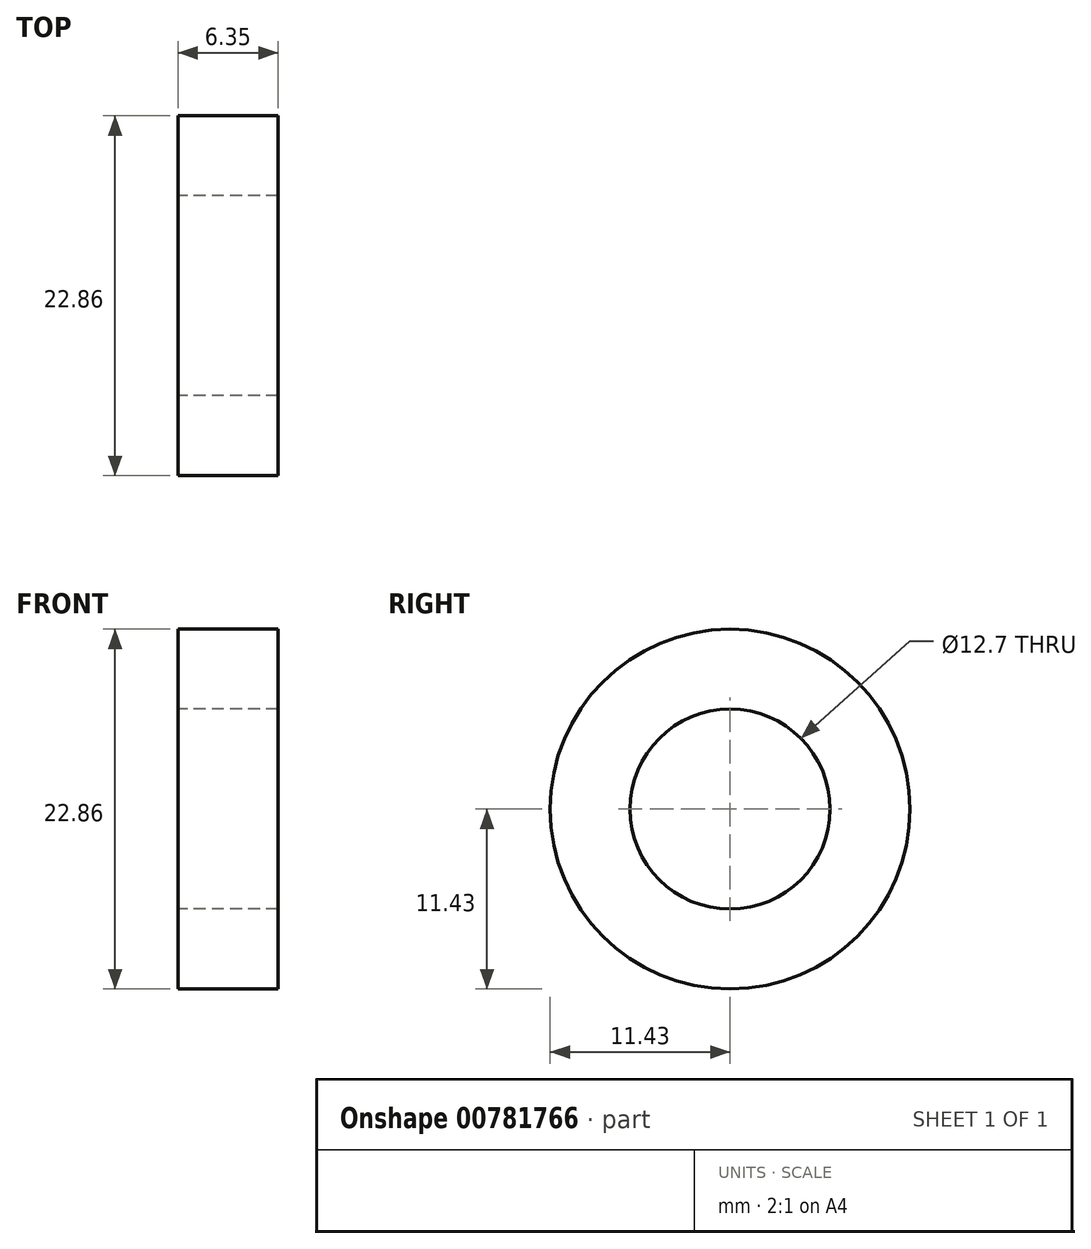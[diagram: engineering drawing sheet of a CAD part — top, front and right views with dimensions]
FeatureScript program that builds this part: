
annotation { "Feature Type Name" : "Feature", "Feature Type Description" : "" }
export const myFeature = defineFeature(function(context is Context, id is Id, definition is map)
    precondition{}
    {
        {
            var Q0;
            Q0=qCreatedBy(makeId("Top.planeOp"),FACE);
            var sketch = newSketch(context, id + "F0", { "sketchPlane" : qUnion([Q0])});
            skLineSegment(sketch, "E0.bottom", {"start": v(31.75, -31.75) * mm, "end": v(-31.75, -31.75) * mm});
            skLineSegment(sketch, "E0.top", {"start": v(31.75, 31.75) * mm, "end": v(-31.75, 31.75) * mm});
            skLineSegment(sketch, "E0.left", {"start": v(31.75, -31.75) * mm, "end": v(31.75, 31.75) * mm});
            skLineSegment(sketch, "E0.right", {"start": v(-31.75, -31.75) * mm, "end": v(-31.75, 31.75) * mm});
            skPoint(sketch, "E0.middle", {"position": v(0, 0) * mm});
            skLineSegment(sketch, "E1.bottom", {"start": v(25.4, -25.4) * mm, "end": v(-25.4, -25.4) * mm});
            skLineSegment(sketch, "E1.top", {"start": v(25.4, 25.4) * mm, "end": v(-25.4, 25.4) * mm});
            skLineSegment(sketch, "E1.left", {"start": v(25.4, -25.4) * mm, "end": v(25.4, 25.4) * mm});
            skLineSegment(sketch, "E1.right", {"start": v(-25.4, -25.4) * mm, "end": v(-25.4, 25.4) * mm});
            skSolve(sketch);
        }
        {
            var Q0;
            Q0=makeQuery(id+"F0.imprint","IMPRINT",FACE,{"disambiguationData":[TD([[makeQuery(id+"F0.imprint","IMPRINT",EDGE,{"derivedFrom":sQuery(id+"F0.wireOp",EDGE,"E0.bottom")}),-1.0]])]});
            extrude(context, id + "F1", {"entities" : qUnion([Q0]), "endBound" : BoundingType.SYMMETRIC, "depth" : 330.2 * mm, "offsetDistance" : 25.4 * mm});
        }
        {
            var Q0;
            Q0=makeQuery(id+"F1.opExtrude","SWEPT_FACE",FACE,{"disambiguationData":[OSD([sQuery(id+"F0.wireOp",EDGE,"E0.right")])]});
            var sketch = newSketch(context, id + "F2", { "sketchPlane" : qUnion([Q0])});
            skSolve(sketch);
        }
        {
            var Q0;
            Q0=makeQuery(id+"F1.opExtrude","SWEPT_FACE",FACE,{"disambiguationData":[OSD([sQuery(id+"F0.wireOp",EDGE,"E0.left")])]});
            var sketch = newSketch(context, id + "F3", { "sketchPlane" : qUnion([Q0])});
            skLineSegment(sketch, "E2.0", {"start": v(-31.75, 165.1) * mm, "end": v(31.75, 165.1) * mm, "construction": true});
            skLineSegment(sketch, "E2.1", {"start": v(-31.75, 165.1) * mm, "end": v(-31.75, -165.1) * mm, "construction": true});
            skLineSegment(sketch, "E2.2", {"start": v(31.75, 165.1) * mm, "end": v(31.75, -165.1) * mm, "construction": true});
            skLineSegment(sketch, "E2.3", {"start": v(-31.75, -165.1) * mm, "end": v(31.75, -165.1) * mm, "construction": true});
            skCircle(sketch, "E3", {"center": v(0, 146.05) * mm, "radius": 6.35 * mm});
            skArc(sketch, "E4", {"start": v(17.84, 137.73) * mm, "mid": v(19.5, 143.31) * mm, "end": v(19.44, 149.13) * mm});
            skArc(sketch, "E5", {"start": v(10.93, 140.95) * mm, "mid": v(11.95, 144.37) * mm, "end": v(11.92, 147.94) * mm});
            skLineSegment(sketch, "E6", {"start": v(0, 146.05) * mm, "end": v(19.44, 149.13) * mm, "construction": true});
            skLineSegment(sketch, "E7", {"start": v(0, 146.05) * mm, "end": v(9.54, 128.83) * mm, "construction": true});
            skLineSegment(sketch, "E8", {"start": v(0, 146.05) * mm, "end": v(24.19, 134.77) * mm, "construction": true});
            skCircle(sketch, "E9", {"center": v(0, 146.05) * mm, "radius": 15.88 * mm, "construction": true});
            skArc(sketch, "E10", {"start": v(11.92, 147.94) * mm, "mid": v(15.08, 152.3) * mm, "end": v(19.44, 149.13) * mm});
            skArc(sketch, "E11.MirrorCS", {"start": v(6.21, 135.7) * mm, "mid": v(4.91, 130.48) * mm, "end": v(10.14, 129.18) * mm});
            skArc(sketch, "E12.MirrorCS", {"start": v(10.93, 140.95) * mm, "mid": v(8.97, 137.98) * mm, "end": v(6.21, 135.7) * mm});
            skArc(sketch, "E13.MirrorCS", {"start": v(17.84, 137.73) * mm, "mid": v(14.63, 132.88) * mm, "end": v(10.14, 129.18) * mm});
            skLineSegment(sketch, "E14", {"start": v(0, 146.05) * mm, "end": v(-19.11, 146.05) * mm, "construction": true});
            skLineSegment(sketch, "E15", {"start": v(0, 146.05) * mm, "end": v(0, 119.4) * mm, "construction": true});
            skArc(sketch, "E16.MirrorCS", {"start": v(-6.21, 135.7) * mm, "mid": v(-4.91, 130.48) * mm, "end": v(-10.14, 129.18) * mm});
            skArc(sketch, "E17.MirrorCS", {"start": v(-17.84, 137.73) * mm, "mid": v(-14.63, 132.88) * mm, "end": v(-10.14, 129.18) * mm});
            skArc(sketch, "E18.MirrorCS", {"start": v(-17.84, 137.73) * mm, "mid": v(-19.5, 143.31) * mm, "end": v(-19.44, 149.13) * mm});
            skArc(sketch, "E19.MirrorCS", {"start": v(-11.92, 147.94) * mm, "mid": v(-15.08, 152.3) * mm, "end": v(-19.44, 149.13) * mm});
            skArc(sketch, "E20.MirrorCS", {"start": v(-10.93, 140.95) * mm, "mid": v(-11.95, 144.37) * mm, "end": v(-11.92, 147.94) * mm});
            skArc(sketch, "E21.MirrorCS", {"start": v(-10.93, 140.95) * mm, "mid": v(-8.97, 137.98) * mm, "end": v(-6.21, 135.7) * mm});
            skSolve(sketch);
        }
        {
            var Q0;
            Q0=makeQuery(id+"F3.imprint","IMPRINT",FACE,{"disambiguationData":[TD([[makeQuery(id+"F3.imprint","IMPRINT",EDGE,{"derivedFrom":sQuery(id+"F3.wireOp",EDGE,"E3")}),1.0]])]});
            var Q1;
            Q1=makeQuery(id+"F3.imprint","IMPRINT",FACE,{"disambiguationData":[TD([[makeQuery(id+"F3.imprint","IMPRINT",EDGE,{"derivedFrom":sQuery(id+"F3.wireOp",EDGE,"E4")}),1.0]])]});
            var Q2;
            Q2=makeQuery(id+"F3.imprint","IMPRINT",FACE,{"disambiguationData":[TD([[makeQuery(id+"F3.imprint","IMPRINT",EDGE,{"derivedFrom":sQuery(id+"F3.wireOp",EDGE,"E16.MirrorCS")}),-1.0]])]});
            extrude(context, id + "F4", {"entities" : qUnion([Q0, Q1, Q2]), "operationType" : NewBodyOperationType.REMOVE, "oppositeDirection" : true, "depth" : 25.4 * mm, "offsetDistance" : 25.4 * mm});
        }
        {
            var Q0;
            {var subQ0=sQuery(id+"F0.wireOp",EDGE,"E0.right");Q0=makeQuery(id+"F2.imprint","IMPRINT",FACE,{"disambiguationData":[TD([[makeQuery(id+"F2.imprint","IMPRINT",EDGE,{"derivedFrom":makeQuery(id+"F1.opExtrude","CAP_EDGE",EDGE,{"disambiguationData":[OSD([subQ0])],"isStart":true})}),-1.0]])]});}
            var sketch = newSketch(context, id + "F5", { "sketchPlane" : qUnion([Q0])});
            skCircle(sketch, "E22.0", {"center": v(0, 146.05) * mm, "radius": 6.35 * mm});
            skCircle(sketch, "E23", {"center": v(-7.7, 132.17) * mm, "radius": 1.9 * mm});
            skArc(sketch, "E24", {"start": v(5.1, 127.04) * mm, "mid": v(17.84, 137.73) * mm, "end": v(17.84, 154.37) * mm});
            skCircle(sketch, "E25", {"center": v(0, 146.05) * mm, "radius": 15.88 * mm, "construction": true});
            skLineSegment(sketch, "E26", {"start": v(0, 146.05) * mm, "end": v(5.1, 127.04) * mm, "construction": true});
            skLineSegment(sketch, "E27", {"start": v(0, 146.05) * mm, "end": v(-15.88, 146.05) * mm, "construction": true});
            skLineSegment(sketch, "E28", {"start": v(0, 146.05) * mm, "end": v(17.84, 154.37) * mm, "construction": true});
            skArc(sketch, "E29", {"start": v(3.12, 134.4) * mm, "mid": v(10.93, 140.95) * mm, "end": v(10.93, 151.15) * mm});
            skLineSegment(sketch, "E30", {"start": v(0, 146.05) * mm, "end": v(-7.7, 132.17) * mm});
            skArc(sketch, "E31", {"start": v(3.12, 134.4) * mm, "mid": v(0.43, 129.73) * mm, "end": v(5.1, 127.04) * mm});
            skArc(sketch, "E32", {"start": v(17.84, 154.37) * mm, "mid": v(12.78, 156.21) * mm, "end": v(10.93, 151.15) * mm});
            skCircle(sketch, "E33", {"center": v(-7.7, 132.17) * mm, "radius": 3.18 * mm, "construction": true});
            skLineSegment(sketch, "E34", {"start": v(0, 146.05) * mm, "end": v(-15.58, 149.08) * mm, "construction": true});
            skCircle(sketch, "E35", {"center": v(-15.58, 149.08) * mm, "radius": 3.18 * mm, "construction": true});
            skArc(sketch, "E36.0", {"start": v(-11.92, 147.94) * mm, "mid": v(-15.08, 152.3) * mm, "end": v(-19.44, 149.13) * mm, "construction": true});
            skLineSegment(sketch, "E37", {"start": v(0, 146.05) * mm, "end": v(-15.68, 148.53) * mm, "construction": true});
            skSolve(sketch);
        }
        {
            var Q0;
            Q0=qSketchRegion(id+"F5",true);
            extrude(context, id + "F6", {"entities" : qUnion([Q0]), "operationType" : NewBodyOperationType.REMOVE, "oppositeDirection" : true, "depth" : 25.4 * mm, "offsetDistance" : 25.4 * mm});
        }
        {
            var Q0;
            Q0=makeQuery(id+"F1.opExtrude","SWEPT_FACE",FACE,{"disambiguationData":[OSD([sQuery(id+"F0.wireOp",EDGE,"E0.left")])]});
            var sketch = newSketch(context, id + "F7", { "sketchPlane" : qUnion([Q0])});
            skArc(sketch, "E38", {"start": v(-8.89, 101.6) * mm, "mid": v(10.16, 82.55) * mm, "end": v(-8.89, 63.5) * mm, "construction": true});
            skArc(sketch, "E39.0", {"start": v(-8.89, 95.25) * mm, "mid": v(3.81, 82.55) * mm, "end": v(-8.89, 69.85) * mm});
            skArc(sketch, "E40.0", {"start": v(-8.89, 107.95) * mm, "mid": v(16.5, 82.55) * mm, "end": v(-8.89, 57.15) * mm});
            skArc(sketch, "E41", {"start": v(-8.89, 107.95) * mm, "mid": v(-15.24, 101.6) * mm, "end": v(-8.89, 95.25) * mm});
            skArc(sketch, "E42", {"start": v(-8.89, 57.15) * mm, "mid": v(-15.24, 63.5) * mm, "end": v(-8.89, 69.85) * mm});
            skArc(sketch, "E43", {"start": v(8.9, 6.35) * mm, "mid": v(-10.16, 25.4) * mm, "end": v(8.9, 44.45) * mm, "construction": true});
            skArc(sketch, "E44.0", {"start": v(8.9, 12.7) * mm, "mid": v(-3.8, 25.4) * mm, "end": v(8.9, 38.1) * mm});
            skArc(sketch, "E45.0", {"start": v(8.9, 0) * mm, "mid": v(-16.5, 25.4) * mm, "end": v(8.89, 50.8) * mm});
            skArc(sketch, "E46", {"start": v(8.9, 0) * mm, "mid": v(15.24, 6.35) * mm, "end": v(8.9, 12.7) * mm});
            skArc(sketch, "E47", {"start": v(8.9, 50.8) * mm, "mid": v(15.24, 44.45) * mm, "end": v(8.9, 38.1) * mm});
            skArc(sketch, "E48", {"start": v(-8.89, -12.7) * mm, "mid": v(10.16, -31.75) * mm, "end": v(-8.89, -50.8) * mm, "construction": true});
            skArc(sketch, "E49.0", {"start": v(-8.89, -19.05) * mm, "mid": v(3.81, -31.75) * mm, "end": v(-8.89, -44.45) * mm});
            skArc(sketch, "E50.0", {"start": v(-8.89, -6.35) * mm, "mid": v(16.5, -31.75) * mm, "end": v(-8.89, -57.15) * mm});
            skArc(sketch, "E51", {"start": v(-8.89, -6.35) * mm, "mid": v(-15.24, -12.7) * mm, "end": v(-8.89, -19.05) * mm});
            skArc(sketch, "E52", {"start": v(-8.89, -57.15) * mm, "mid": v(-15.24, -50.8) * mm, "end": v(-8.89, -44.45) * mm});
            skArc(sketch, "E53", {"start": v(8.9, -107.95) * mm, "mid": v(-10.16, -88.9) * mm, "end": v(8.89, -69.85) * mm, "construction": true});
            skArc(sketch, "E54.0", {"start": v(8.9, -101.6) * mm, "mid": v(-3.8, -88.9) * mm, "end": v(8.89, -76.2) * mm});
            skArc(sketch, "E55.0", {"start": v(8.9, -114.3) * mm, "mid": v(-16.5, -88.9) * mm, "end": v(8.89, -63.5) * mm});
            skArc(sketch, "E56", {"start": v(8.9, -114.3) * mm, "mid": v(15.24, -107.95) * mm, "end": v(8.9, -101.6) * mm});
            skArc(sketch, "E57", {"start": v(8.89, -63.5) * mm, "mid": v(15.24, -69.85) * mm, "end": v(8.89, -76.2) * mm});
            skCircle(sketch, "E58", {"center": v(-8.89, 82.55) * mm, "radius": 6.35 * mm});
            skCircle(sketch, "E59", {"center": v(8.9, 25.4) * mm, "radius": 6.35 * mm});
            skCircle(sketch, "E60", {"center": v(8.9, -88.9) * mm, "radius": 6.35 * mm});
            skCircle(sketch, "E61", {"center": v(-8.89, -31.75) * mm, "radius": 6.35 * mm});
            skSolve(sketch);
        }
        {
            var Q0;
            Q0=qSketchRegion(id+"F7",true);
            extrude(context, id + "F8", {"entities" : qUnion([Q0]), "operationType" : NewBodyOperationType.REMOVE, "endBound" : BoundingType.THROUGH_ALL, "oppositeDirection" : true, "depth" : 25.4 * mm, "offsetDistance" : 25.4 * mm});
        }
        {
            var Q0;
            Q0=makeQuery(id+"F1.opExtrude","SWEPT_FACE",FACE,{"disambiguationData":[OSD([sQuery(id+"F0.wireOp",EDGE,"E1.left")])]});
            var sketch = newSketch(context, id + "F9", { "sketchPlane" : qUnion([Q0])});
            skLineSegment(sketch, "E62.bottom", {"start": v(-25.4, 165.1) * mm, "end": v(25.4, 165.1) * mm});
            skLineSegment(sketch, "E62.top", {"start": v(-25.4, -127) * mm, "end": v(25.4, -127) * mm});
            skLineSegment(sketch, "E62.left", {"start": v(-25.4, 165.1) * mm, "end": v(-25.4, -127) * mm});
            skLineSegment(sketch, "E62.right", {"start": v(25.4, 165.1) * mm, "end": v(25.4, -127) * mm});
            skLineSegment(sketch, "E63.bottom", {"start": v(72.9, -188.97) * mm, "end": v(-72.9, -188.97) * mm});
            skLineSegment(sketch, "E63.top", {"start": v(72.9, 188.97) * mm, "end": v(-72.9, 188.97) * mm});
            skLineSegment(sketch, "E63.left", {"start": v(72.9, -188.97) * mm, "end": v(72.9, 188.97) * mm});
            skLineSegment(sketch, "E63.right", {"start": v(-72.9, -188.97) * mm, "end": v(-72.9, 188.97) * mm});
            skPoint(sketch, "E63.middle", {"position": v(0, 0) * mm});
            skSolve(sketch);
        }
        {
            var Q0;
            Q0=qSketchRegion(id+"F9",true);
            extrude(context, id + "F10", {"entities" : qUnion([Q0]), "operationType" : NewBodyOperationType.REMOVE, "endBound" : BoundingType.SYMMETRIC, "oppositeDirection" : true, "depth" : 127 * mm, "offsetDistance" : 25.4 * mm});
        }
        {
            var Q0;
            Q0=makeQuery(id+"F1.opExtrude","SWEPT_FACE",FACE,{"disambiguationData":[OSD([sQuery(id+"F0.wireOp",EDGE,"E1.right")])]});
            var sketch = newSketch(context, id + "F11", { "sketchPlane" : qUnion([Q0])});
            skLineSegment(sketch, "E64.bottom", {"start": v(-48.84, -169.45) * mm, "end": v(48.84, -169.45) * mm});
            skLineSegment(sketch, "E64.top", {"start": v(-48.84, 169.45) * mm, "end": v(48.84, 169.45) * mm});
            skLineSegment(sketch, "E64.left", {"start": v(-48.84, -169.45) * mm, "end": v(-48.84, 169.45) * mm});
            skLineSegment(sketch, "E64.right", {"start": v(48.84, -169.45) * mm, "end": v(48.84, 169.45) * mm});
            skPoint(sketch, "E64.middle", {"position": v(0, 0) * mm});
            skSolve(sketch);
        }
        {
            var Q0;
            Q0=qSketchRegion(id+"F11",true);
            extrude(context, id + "F12", {"entities" : qUnion([Q0]), "operationType" : NewBodyOperationType.REMOVE, "endBound" : BoundingType.THROUGH_ALL, "depth" : 25.4 * mm, "offsetDistance" : 25.4 * mm});
        }
        {
            var Q0;
            {var subQ0=sQuery(id+"F0.wireOp",EDGE,"E0.right");Q0=makeQuery(id+"F2.imprint","IMPRINT",FACE,{"disambiguationData":[TD([[makeQuery(id+"F2.imprint","IMPRINT",EDGE,{"derivedFrom":makeQuery(id+"F1.opExtrude","CAP_EDGE",EDGE,{"disambiguationData":[OSD([subQ0])],"isStart":true})}),-1.0]])]});}
            var sketch = newSketch(context, id + "F13", { "sketchPlane" : qUnion([Q0])});
            skCircle(sketch, "E65", {"center": v(0, 146.05) * mm, "radius": 11.43 * mm});
            skCircle(sketch, "E66.0", {"center": v(0, 146.05) * mm, "radius": 6.35 * mm});
            skSolve(sketch);
        }
        {
            var Q0;
            Q0 = qSketchRegion(id + "F13", true);
            extrude(context, id + "F14", {"entities" : qUnion([Q0]), "operationType" : NewBodyOperationType.ADD, "depth" : 6.35 * mm, "offsetDistance" : 25.4 * mm});
        }
        {
            var Q0;
            {var subQ0=sQuery(id+"F0.wireOp",EDGE,"E0.right");Q0=makeQuery(id+"F2.imprint","IMPRINT",FACE,{"disambiguationData":[TD([[makeQuery(id+"F2.imprint","IMPRINT",EDGE,{"derivedFrom":makeQuery(id+"F1.opExtrude","CAP_EDGE",EDGE,{"disambiguationData":[OSD([subQ0])],"isStart":true})}),-1.0]])]});}
            var sketch = newSketch(context, id + "F15", { "sketchPlane" : qUnion([Q0])});
            skLineSegment(sketch, "E67.bottom", {"start": v(85.4, -173.56) * mm, "end": v(-85.4, -173.56) * mm});
            skLineSegment(sketch, "E67.top", {"start": v(85.4, 173.56) * mm, "end": v(-85.4, 173.56) * mm});
            skLineSegment(sketch, "E67.left", {"start": v(85.4, -173.56) * mm, "end": v(85.4, 173.56) * mm});
            skLineSegment(sketch, "E67.right", {"start": v(-85.4, -173.56) * mm, "end": v(-85.4, 173.56) * mm});
            skPoint(sketch, "E67.middle", {"position": v(0, 0) * mm});
            skSolve(sketch);
        }
        {
            var Q0;
            Q0 = qSketchRegion(id + "F15", true);
            extrude(context, id + "F16", {"entities" : qUnion([Q0]), "operationType" : NewBodyOperationType.REMOVE, "oppositeDirection" : true, "depth" : 25.4 * mm, "offsetDistance" : 25.4 * mm});
        }
    });
